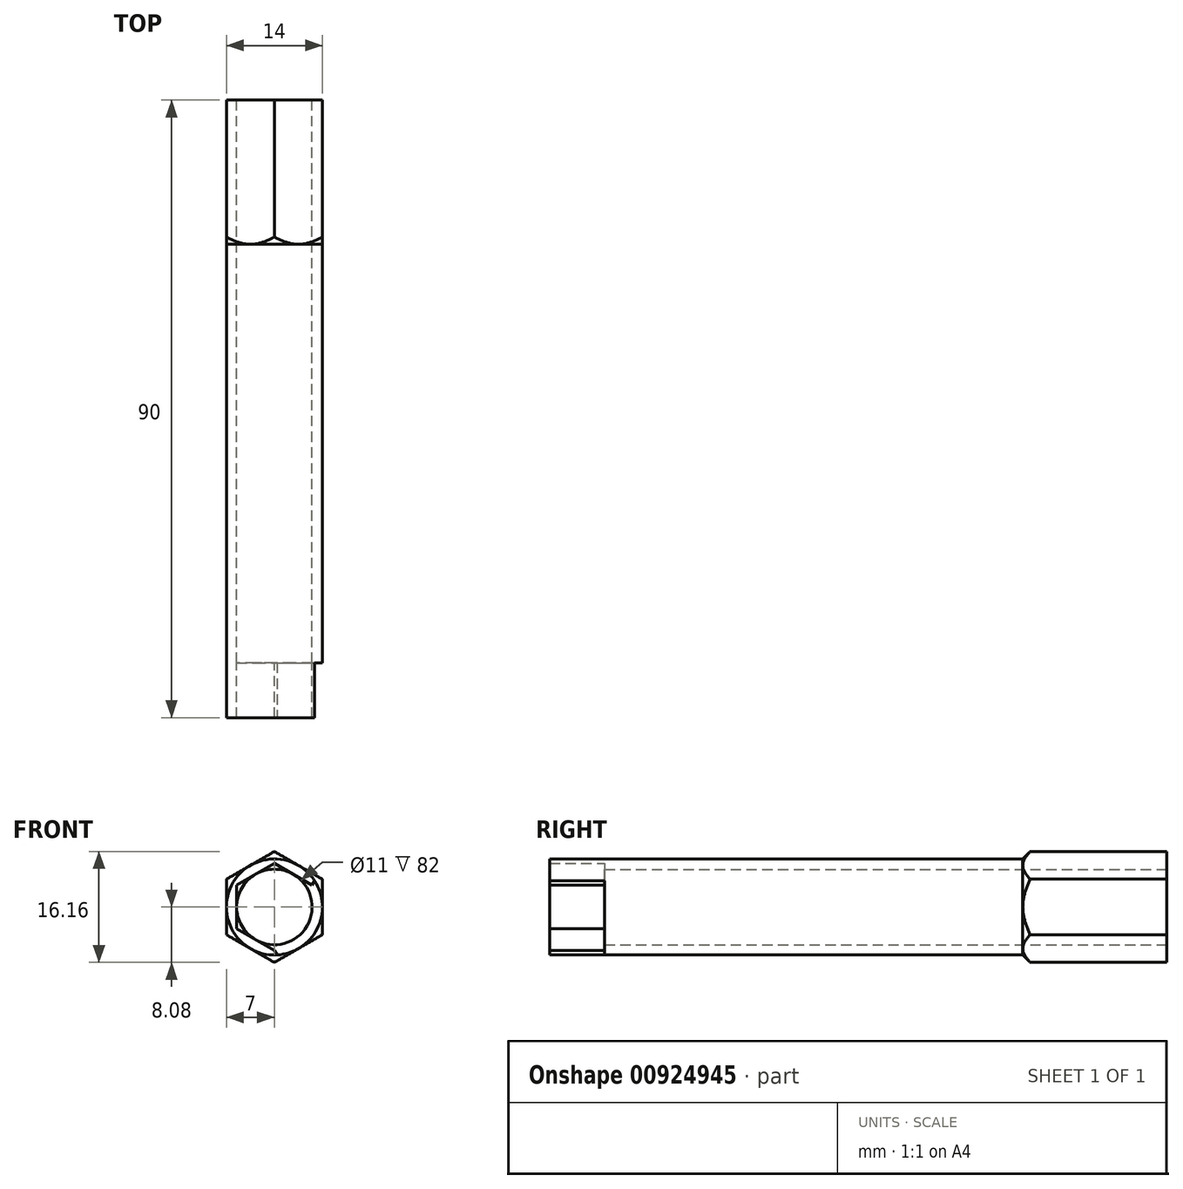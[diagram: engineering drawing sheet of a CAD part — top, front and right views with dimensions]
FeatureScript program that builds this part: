
annotation { "Feature Type Name" : "Feature", "Feature Type Description" : "" }
export const myFeature = defineFeature(function(context is Context, id is Id, definition is map)
    precondition{}
    {
        {
            var Q0;
            Q0=qCreatedBy(makeId("Front.planeOp"),FACE);
            var sketch = newSketch(context, id + "F0", { "sketchPlane" : qUnion([Q0])});
            skCircle(sketch, "E0.cCircle", {"center": v(0, 0) * mm, "radius": 5.5 * mm, "construction": true});
            skLineSegment(sketch, "E0.0", {"start": v(5.5, 3.18) * mm, "end": v(5.5, -3.18) * mm});
            skLineSegment(sketch, "E0.1", {"start": v(5.5, -3.18) * mm, "end": v(0, -6.35) * mm});
            skLineSegment(sketch, "E0.2", {"start": v(0, -6.35) * mm, "end": v(-5.5, -3.18) * mm});
            skLineSegment(sketch, "E0.3", {"start": v(-5.5, -3.18) * mm, "end": v(-5.5, 3.18) * mm});
            skLineSegment(sketch, "E0.4", {"start": v(-5.5, 3.18) * mm, "end": v(0, 6.35) * mm});
            skLineSegment(sketch, "E0.5", {"start": v(0, 6.35) * mm, "end": v(5.5, 3.18) * mm});
            skPoint(sketch, "E0.0.midPoint", {"position": v(5.5, 0) * mm});
            skLineSegment(sketch, "E1", {"start": v(-5.5, 3.18) * mm, "end": v(0, -6.35) * mm, "construction": true});
            skCircle(sketch, "E2", {"center": v(0, 0) * mm, "radius": 7 * mm});
            skLineSegment(sketch, "E3", {"start": v(5.5, 0) * mm, "end": v(7, 0) * mm, "construction": true});
            skCircle(sketch, "E4", {"center": v(0, 0) * mm, "radius": 5.5 * mm});
            skSolve(sketch);
        }
        {
            var Q0;
            Q0=makeQuery(id+"F0.imprint","IMPRINT",FACE,{"disambiguationData":[TD([[makeQuery(id+"F0.imprint","IMPRINT",EDGE,{"derivedFrom":sQuery(id+"F0.wireOp",EDGE,"E0.0")}),1.0]])]});
            extrude(context, id + "F1", {"entities" : qUnion([Q0]), "depth" : 70 * mm, "offsetDistance" : 25 * mm});
        }
        {
            var Q0;
            {var subQ0=sQuery(id+"F0.wireOp",EDGE,"E0.1");var subQ1=sQuery(id+"F0.wireOp",EDGE,"E0.0");var subQ2=makeQuery(id+"F0.imprint","INTERSECT",VERTEX,{"derivedFrom":[subQ1,subQ0]});Q0=makeQuery(id+"F0.imprint","IMPRINT",FACE,{"disambiguationData":[TD([[makeQuery(id+"F0.imprint","IMPRINT",EDGE,{"disambiguationData":[TD([[subQ2,1.0]])],"derivedFrom":subQ1}),-1.0]])]});}
            var Q1;
            {var subQ0=sQuery(id+"F0.wireOp",EDGE,"E0.2");var subQ1=sQuery(id+"F0.wireOp",EDGE,"E0.1");var subQ2=makeQuery(id+"F0.imprint","INTERSECT",VERTEX,{"derivedFrom":[subQ1,subQ0]});Q1=makeQuery(id+"F0.imprint","IMPRINT",FACE,{"disambiguationData":[TD([[makeQuery(id+"F0.imprint","IMPRINT",EDGE,{"disambiguationData":[TD([[subQ2,1.0]])],"derivedFrom":subQ1}),-1.0]])]});}
            var Q2;
            {var subQ0=sQuery(id+"F0.wireOp",EDGE,"E0.3");var subQ1=sQuery(id+"F0.wireOp",EDGE,"E0.2");var subQ2=makeQuery(id+"F0.imprint","INTERSECT",VERTEX,{"derivedFrom":[subQ1,subQ0]});Q2=makeQuery(id+"F0.imprint","IMPRINT",FACE,{"disambiguationData":[TD([[makeQuery(id+"F0.imprint","IMPRINT",EDGE,{"disambiguationData":[TD([[subQ2,1.0]])],"derivedFrom":subQ1}),-1.0]])]});}
            var Q3;
            {var subQ0=sQuery(id+"F0.wireOp",EDGE,"E0.4");var subQ1=sQuery(id+"F0.wireOp",EDGE,"E0.3");var subQ2=makeQuery(id+"F0.imprint","INTERSECT",VERTEX,{"derivedFrom":[subQ1,subQ0]});Q3=makeQuery(id+"F0.imprint","IMPRINT",FACE,{"disambiguationData":[TD([[makeQuery(id+"F0.imprint","IMPRINT",EDGE,{"disambiguationData":[TD([[subQ2,1.0]])],"derivedFrom":subQ1}),-1.0]])]});}
            var Q4;
            {var subQ0=sQuery(id+"F0.wireOp",EDGE,"E0.5");var subQ1=sQuery(id+"F0.wireOp",EDGE,"E0.4");var subQ2=makeQuery(id+"F0.imprint","INTERSECT",VERTEX,{"derivedFrom":[subQ1,subQ0]});Q4=makeQuery(id+"F0.imprint","IMPRINT",FACE,{"disambiguationData":[TD([[makeQuery(id+"F0.imprint","IMPRINT",EDGE,{"disambiguationData":[TD([[subQ2,1.0]])],"derivedFrom":subQ1}),-1.0]])]});}
            var Q5;
            {var subQ0=sQuery(id+"F0.wireOp",EDGE,"E0.5");var subQ1=sQuery(id+"F0.wireOp",EDGE,"E0.0");var subQ2=makeQuery(id+"F0.imprint","INTERSECT",VERTEX,{"derivedFrom":[subQ1,subQ0]});Q5=makeQuery(id+"F0.imprint","IMPRINT",FACE,{"disambiguationData":[TD([[makeQuery(id+"F0.imprint","IMPRINT",EDGE,{"disambiguationData":[TD([[subQ2,-1.0]])],"derivedFrom":subQ1}),-1.0]])]});}
            extrude(context, id + "F2", {"entities" : qUnion([Q0, Q1, Q2, Q3, Q4, Q5]), "operationType" : NewBodyOperationType.ADD, "depth" : 62 * mm, "offsetDistance" : 25 * mm});
        }
        {
            var Q0;
            {var subQ0=sQuery(id+"F0.wireOp",EDGE,"E4");var subQ1=sQuery(id+"F0.wireOp",EDGE,"E0.5");var subQ2=sQuery(id+"F0.wireOp",EDGE,"E0.4");var subQ3=sQuery(id+"F0.wireOp",EDGE,"E0.3");var subQ4=sQuery(id+"F0.wireOp",EDGE,"E0.2");var subQ5=sQuery(id+"F0.wireOp",EDGE,"E0.1");var subQ6=sQuery(id+"F0.wireOp",EDGE,"E0.0");Q0=makeQuery(id+"F2.boolean.opBoolean","MERGE",FACE,{"derivedFrom":[makeQuery(id+"F1.opExtrude","CAP_FACE",FACE,{"disambiguationData":[OSD([subQ6,subQ5,subQ4,subQ3,subQ2,subQ1,sQuery(id+"F0.wireOp",EDGE,"E2")])],"isStart":true}),makeQuery(id+"F2.opExtrude","CAP_FACE",FACE,{"disambiguationData":[OSD([subQ6,subQ1,subQ0])],"isStart":true}),makeQuery(id+"F2.opExtrude","CAP_FACE",FACE,{"disambiguationData":[OSD([subQ6,subQ5,subQ0])],"isStart":true}),makeQuery(id+"F2.opExtrude","CAP_FACE",FACE,{"disambiguationData":[OSD([subQ5,subQ4,subQ0])],"isStart":true}),makeQuery(id+"F2.opExtrude","CAP_FACE",FACE,{"disambiguationData":[OSD([subQ4,subQ3,subQ0])],"isStart":true}),makeQuery(id+"F2.opExtrude","CAP_FACE",FACE,{"disambiguationData":[OSD([subQ3,subQ2,subQ0])],"isStart":true}),makeQuery(id+"F2.opExtrude","CAP_FACE",FACE,{"disambiguationData":[OSD([subQ2,subQ1,subQ0])],"isStart":true})]});}
            var sketch = newSketch(context, id + "F3", { "sketchPlane" : qUnion([Q0])});
            skCircle(sketch, "E5.cCircle", {"center": v(0, 0) * mm, "radius": 7 * mm, "construction": true});
            skLineSegment(sketch, "E5.0", {"start": v(-7, -4.04) * mm, "end": v(-7, 4.04) * mm});
            skLineSegment(sketch, "E5.1", {"start": v(-7, 4.04) * mm, "end": v(0, 8.08) * mm});
            skLineSegment(sketch, "E5.2", {"start": v(0, 8.08) * mm, "end": v(7, 4.04) * mm});
            skLineSegment(sketch, "E5.3", {"start": v(7, 4.04) * mm, "end": v(7, -4.04) * mm});
            skLineSegment(sketch, "E5.4", {"start": v(7, -4.04) * mm, "end": v(0, -8.08) * mm});
            skLineSegment(sketch, "E5.5", {"start": v(0, -8.08) * mm, "end": v(-7, -4.04) * mm});
            skPoint(sketch, "E5.0.midPoint", {"position": v(-7, 0) * mm});
            skCircle(sketch, "E6.0", {"center": v(0, 0) * mm, "radius": 5.5 * mm});
            skSolve(sketch);
        }
        {
            var Q0;
            Q0=makeQuery(id+"F3.imprint","IMPRINT",FACE,{"disambiguationData":[TD([[makeQuery(id+"F3.imprint","IMPRINT",EDGE,{"derivedFrom":sQuery(id+"F3.wireOp",EDGE,"E6.0")}),1.0]])]});
            var Q1;
            {var subQ0=sQuery(id+"F3.wireOp",EDGE,"E5.1");var subQ1=sQuery(id+"F3.wireOp",EDGE,"E5.0");var subQ2=makeQuery(id+"F3.imprint","INTERSECT",VERTEX,{"derivedFrom":[subQ1,subQ0]});Q1=makeQuery(id+"F3.imprint","IMPRINT",FACE,{"disambiguationData":[TD([[makeQuery(id+"F3.imprint","IMPRINT",EDGE,{"disambiguationData":[TD([[subQ2,1.0]])],"derivedFrom":subQ1}),-1.0]])]});}
            var Q2;
            {var subQ0=sQuery(id+"F3.wireOp",EDGE,"E5.2");var subQ1=sQuery(id+"F3.wireOp",EDGE,"E5.1");var subQ2=makeQuery(id+"F3.imprint","INTERSECT",VERTEX,{"derivedFrom":[subQ1,subQ0]});Q2=makeQuery(id+"F3.imprint","IMPRINT",FACE,{"disambiguationData":[TD([[makeQuery(id+"F3.imprint","IMPRINT",EDGE,{"disambiguationData":[TD([[subQ2,1.0]])],"derivedFrom":subQ1}),-1.0]])]});}
            var Q3;
            {var subQ0=sQuery(id+"F3.wireOp",EDGE,"E5.3");var subQ1=sQuery(id+"F3.wireOp",EDGE,"E5.2");var subQ2=makeQuery(id+"F3.imprint","INTERSECT",VERTEX,{"derivedFrom":[subQ1,subQ0]});Q3=makeQuery(id+"F3.imprint","IMPRINT",FACE,{"disambiguationData":[TD([[makeQuery(id+"F3.imprint","IMPRINT",EDGE,{"disambiguationData":[TD([[subQ2,1.0]])],"derivedFrom":subQ1}),-1.0]])]});}
            var Q4;
            {var subQ0=sQuery(id+"F3.wireOp",EDGE,"E5.4");var subQ1=sQuery(id+"F3.wireOp",EDGE,"E5.3");var subQ2=makeQuery(id+"F3.imprint","INTERSECT",VERTEX,{"derivedFrom":[subQ1,subQ0]});Q4=makeQuery(id+"F3.imprint","IMPRINT",FACE,{"disambiguationData":[TD([[makeQuery(id+"F3.imprint","IMPRINT",EDGE,{"disambiguationData":[TD([[subQ2,1.0]])],"derivedFrom":subQ1}),-1.0]])]});}
            var Q5;
            {var subQ0=sQuery(id+"F3.wireOp",EDGE,"E5.5");var subQ1=sQuery(id+"F3.wireOp",EDGE,"E5.4");var subQ2=makeQuery(id+"F3.imprint","INTERSECT",VERTEX,{"derivedFrom":[subQ1,subQ0]});Q5=makeQuery(id+"F3.imprint","IMPRINT",FACE,{"disambiguationData":[TD([[makeQuery(id+"F3.imprint","IMPRINT",EDGE,{"disambiguationData":[TD([[subQ2,1.0]])],"derivedFrom":subQ1}),-1.0]])]});}
            var Q6;
            {var subQ0=sQuery(id+"F3.wireOp",EDGE,"E5.5");var subQ1=sQuery(id+"F3.wireOp",EDGE,"E5.0");var subQ2=makeQuery(id+"F3.imprint","INTERSECT",VERTEX,{"derivedFrom":[subQ1,subQ0]});Q6=makeQuery(id+"F3.imprint","IMPRINT",FACE,{"disambiguationData":[TD([[makeQuery(id+"F3.imprint","IMPRINT",EDGE,{"disambiguationData":[TD([[subQ2,-1.0]])],"derivedFrom":subQ1}),-1.0]])]});}
            extrude(context, id + "F4", {"entities" : qUnion([Q0, Q1, Q2, Q3, Q4, Q5, Q6]), "operationType" : NewBodyOperationType.ADD, "depth" : 20 * mm, "offsetDistance" : 25 * mm});
        }
        {
            var Q0;
            Q0=makeQuery(id+"F1.opExtrude","CAP_FACE",FACE,{"disambiguationData":[OSD([sQuery(id+"F0.wireOp",EDGE,"E0.0"),sQuery(id+"F0.wireOp",EDGE,"E0.1"),sQuery(id+"F0.wireOp",EDGE,"E0.2"),sQuery(id+"F0.wireOp",EDGE,"E0.3"),sQuery(id+"F0.wireOp",EDGE,"E0.4"),sQuery(id+"F0.wireOp",EDGE,"E0.5"),sQuery(id+"F0.wireOp",EDGE,"E2")])],"isStart":false});
            var sketch = newSketch(context, id + "F5", { "sketchPlane" : qUnion([Q0])});
            skLineSegment(sketch, "E7", {"start": v(5.5, -3.18) * mm, "end": v(5.87, -3.81) * mm});
            skLineSegment(sketch, "E8", {"start": v(0, -6.35) * mm, "end": v(0.37, -7) * mm});
            skLineSegment(sketch, "E9", {"start": v(0, 6.35) * mm, "end": v(0.37, 7) * mm});
            skLineSegment(sketch, "E10", {"start": v(5.5, 3.18) * mm, "end": v(5.87, 3.81) * mm});
            skLineSegment(sketch, "E11", {"start": v(-5.5, -3.18) * mm, "end": v(-6.24, -3.18) * mm});
            skLineSegment(sketch, "E12", {"start": v(-5.5, 3.18) * mm, "end": v(-6.24, 3.18) * mm});
            skSolve(sketch);
        }
        {
            var Q0;
            {var subQ0=sQuery(id+"F5.wireOp",EDGE,"E7");Q0=makeQuery(id+"F5.imprint","IMPRINT",FACE,{"disambiguationData":[TD([[makeQuery(id+"F5.imprint","IMPRINT",EDGE,{"derivedFrom":subQ0}),1.0]])]});}
            var Q1;
            {var subQ0=sQuery(id+"F5.wireOp",EDGE,"E7");Q1=makeQuery(id+"F5.imprint","IMPRINT",FACE,{"disambiguationData":[TD([[makeQuery(id+"F5.imprint","IMPRINT",EDGE,{"derivedFrom":subQ0}),-1.0]])]});}
            var Q2;
            Q2=makeQuery(id+"F2.opExtrude","CAP_FACE",FACE,{"disambiguationData":[OSD([sQuery(id+"F0.wireOp",EDGE,"E0.0"),sQuery(id+"F0.wireOp",EDGE,"E0.1"),sQuery(id+"F0.wireOp",EDGE,"E4")])],"isStart":false});
            extrude(context, id + "F6", {"entities" : qUnion([Q0, Q1]), "operationType" : NewBodyOperationType.REMOVE, "endBound" : BoundingType.UP_TO_SURFACE, "oppositeDirection" : true, "depth" : 25 * mm, "endBoundEntityFace" : qUnion([Q2]), "offsetDistance" : 25 * mm});
        }
        {
            var Q0;
            {var subQ0=sQuery(id+"F0.wireOp",EDGE,"E2");var subQ1=sQuery(id+"F3.wireOp",EDGE,"E5.4");var subQ2=sQuery(id+"F3.wireOp",EDGE,"E5.3");Q0=makeQuery(id+"F4.boolean.opBoolean","SPLIT",EDGE,{"disambiguationData":[TD([makeQuery(id+"F1.opExtrude","SWEPT_FACE",FACE,{"disambiguationData":[OSD([subQ0])]}),makeQuery(id+"F4.opExtrude","CAP_FACE",FACE,{"disambiguationData":[OSD([sQuery(id+"F3.wireOp",EDGE,"E5.0"),sQuery(id+"F3.wireOp",EDGE,"E5.1"),sQuery(id+"F3.wireOp",EDGE,"E5.2"),subQ2,subQ1,sQuery(id+"F3.wireOp",EDGE,"E5.5"),sQuery(id+"F3.wireOp",EDGE,"E6.0")])],"isStart":true}),makeQuery(id+"F4.opExtrude","SWEPT_FACE",FACE,{"disambiguationData":[OSD([subQ2])]}),makeQuery(id+"F4.opExtrude","SWEPT_FACE",FACE,{"disambiguationData":[OSD([subQ1])]})])],"derivedFrom":makeQuery(id+"F1.opExtrude","CAP_EDGE",EDGE,{"disambiguationData":[OSD([subQ0])],"isStart":true})});}
            var Q1;
            {var subQ0=sQuery(id+"F0.wireOp",EDGE,"E2");var subQ1=sQuery(id+"F3.wireOp",EDGE,"E5.5");var subQ2=sQuery(id+"F3.wireOp",EDGE,"E5.4");Q1=makeQuery(id+"F4.boolean.opBoolean","SPLIT",EDGE,{"disambiguationData":[TD([makeQuery(id+"F1.opExtrude","SWEPT_FACE",FACE,{"disambiguationData":[OSD([subQ0])]}),makeQuery(id+"F4.opExtrude","CAP_FACE",FACE,{"disambiguationData":[OSD([sQuery(id+"F3.wireOp",EDGE,"E5.0"),sQuery(id+"F3.wireOp",EDGE,"E5.1"),sQuery(id+"F3.wireOp",EDGE,"E5.2"),sQuery(id+"F3.wireOp",EDGE,"E5.3"),subQ2,subQ1,sQuery(id+"F3.wireOp",EDGE,"E6.0")])],"isStart":true}),makeQuery(id+"F4.opExtrude","SWEPT_FACE",FACE,{"disambiguationData":[OSD([subQ2])]}),makeQuery(id+"F4.opExtrude","SWEPT_FACE",FACE,{"disambiguationData":[OSD([subQ1])]})])],"derivedFrom":makeQuery(id+"F1.opExtrude","CAP_EDGE",EDGE,{"disambiguationData":[OSD([subQ0])],"isStart":true})});}
            var Q2;
            {var subQ0=sQuery(id+"F0.wireOp",EDGE,"E2");var subQ1=sQuery(id+"F3.wireOp",EDGE,"E5.0");var subQ2=sQuery(id+"F3.wireOp",EDGE,"E5.5");Q2=makeQuery(id+"F4.boolean.opBoolean","SPLIT",EDGE,{"disambiguationData":[TD([makeQuery(id+"F1.opExtrude","SWEPT_FACE",FACE,{"disambiguationData":[OSD([subQ0])]}),makeQuery(id+"F4.opExtrude","SWEPT_FACE",FACE,{"disambiguationData":[OSD([subQ1])]}),makeQuery(id+"F4.opExtrude","CAP_FACE",FACE,{"disambiguationData":[OSD([subQ1,sQuery(id+"F3.wireOp",EDGE,"E5.1"),sQuery(id+"F3.wireOp",EDGE,"E5.2"),sQuery(id+"F3.wireOp",EDGE,"E5.3"),sQuery(id+"F3.wireOp",EDGE,"E5.4"),subQ2,sQuery(id+"F3.wireOp",EDGE,"E6.0")])],"isStart":true}),makeQuery(id+"F4.opExtrude","SWEPT_FACE",FACE,{"disambiguationData":[OSD([subQ2])]})])],"derivedFrom":makeQuery(id+"F1.opExtrude","CAP_EDGE",EDGE,{"disambiguationData":[OSD([subQ0])],"isStart":true})});}
            var Q3;
            {var subQ0=sQuery(id+"F0.wireOp",EDGE,"E2");var subQ1=sQuery(id+"F3.wireOp",EDGE,"E5.1");var subQ2=sQuery(id+"F3.wireOp",EDGE,"E5.0");Q3=makeQuery(id+"F4.boolean.opBoolean","SPLIT",EDGE,{"disambiguationData":[TD([makeQuery(id+"F1.opExtrude","SWEPT_FACE",FACE,{"disambiguationData":[OSD([subQ0])]}),makeQuery(id+"F4.opExtrude","SWEPT_FACE",FACE,{"disambiguationData":[OSD([subQ2])]}),makeQuery(id+"F4.opExtrude","CAP_FACE",FACE,{"disambiguationData":[OSD([subQ2,subQ1,sQuery(id+"F3.wireOp",EDGE,"E5.2"),sQuery(id+"F3.wireOp",EDGE,"E5.3"),sQuery(id+"F3.wireOp",EDGE,"E5.4"),sQuery(id+"F3.wireOp",EDGE,"E5.5"),sQuery(id+"F3.wireOp",EDGE,"E6.0")])],"isStart":true}),makeQuery(id+"F4.opExtrude","SWEPT_FACE",FACE,{"disambiguationData":[OSD([subQ1])]})])],"derivedFrom":makeQuery(id+"F1.opExtrude","CAP_EDGE",EDGE,{"disambiguationData":[OSD([subQ0])],"isStart":true})});}
            var Q4;
            {var subQ0=sQuery(id+"F0.wireOp",EDGE,"E2");var subQ1=sQuery(id+"F3.wireOp",EDGE,"E5.1");var subQ2=sQuery(id+"F3.wireOp",EDGE,"E5.2");Q4=makeQuery(id+"F4.boolean.opBoolean","SPLIT",EDGE,{"disambiguationData":[TD([makeQuery(id+"F1.opExtrude","SWEPT_FACE",FACE,{"disambiguationData":[OSD([subQ0])]}),makeQuery(id+"F4.opExtrude","CAP_FACE",FACE,{"disambiguationData":[OSD([sQuery(id+"F3.wireOp",EDGE,"E5.0"),subQ1,subQ2,sQuery(id+"F3.wireOp",EDGE,"E5.3"),sQuery(id+"F3.wireOp",EDGE,"E5.4"),sQuery(id+"F3.wireOp",EDGE,"E5.5"),sQuery(id+"F3.wireOp",EDGE,"E6.0")])],"isStart":true}),makeQuery(id+"F4.opExtrude","SWEPT_FACE",FACE,{"disambiguationData":[OSD([subQ1])]}),makeQuery(id+"F4.opExtrude","SWEPT_FACE",FACE,{"disambiguationData":[OSD([subQ2])]})])],"derivedFrom":makeQuery(id+"F1.opExtrude","CAP_EDGE",EDGE,{"disambiguationData":[OSD([subQ0])],"isStart":true})});}
            var Q5;
            {var subQ0=sQuery(id+"F0.wireOp",EDGE,"E2");var subQ1=sQuery(id+"F3.wireOp",EDGE,"E5.3");var subQ2=sQuery(id+"F3.wireOp",EDGE,"E5.2");Q5=makeQuery(id+"F4.boolean.opBoolean","SPLIT",EDGE,{"disambiguationData":[TD([makeQuery(id+"F1.opExtrude","SWEPT_FACE",FACE,{"disambiguationData":[OSD([subQ0])]}),makeQuery(id+"F4.opExtrude","CAP_FACE",FACE,{"disambiguationData":[OSD([sQuery(id+"F3.wireOp",EDGE,"E5.0"),sQuery(id+"F3.wireOp",EDGE,"E5.1"),subQ2,subQ1,sQuery(id+"F3.wireOp",EDGE,"E5.4"),sQuery(id+"F3.wireOp",EDGE,"E5.5"),sQuery(id+"F3.wireOp",EDGE,"E6.0")])],"isStart":true}),makeQuery(id+"F4.opExtrude","SWEPT_FACE",FACE,{"disambiguationData":[OSD([subQ2])]}),makeQuery(id+"F4.opExtrude","SWEPT_FACE",FACE,{"disambiguationData":[OSD([subQ1])]})])],"derivedFrom":makeQuery(id+"F1.opExtrude","CAP_EDGE",EDGE,{"disambiguationData":[OSD([subQ0])],"isStart":true})});}
            chamfer(context, id + "F7", {"entities" : qUnion([Q0, Q1, Q2, Q3, Q4, Q5]), "width" : 1 * mm, "tangentPropagation" : true});
        }
    });
